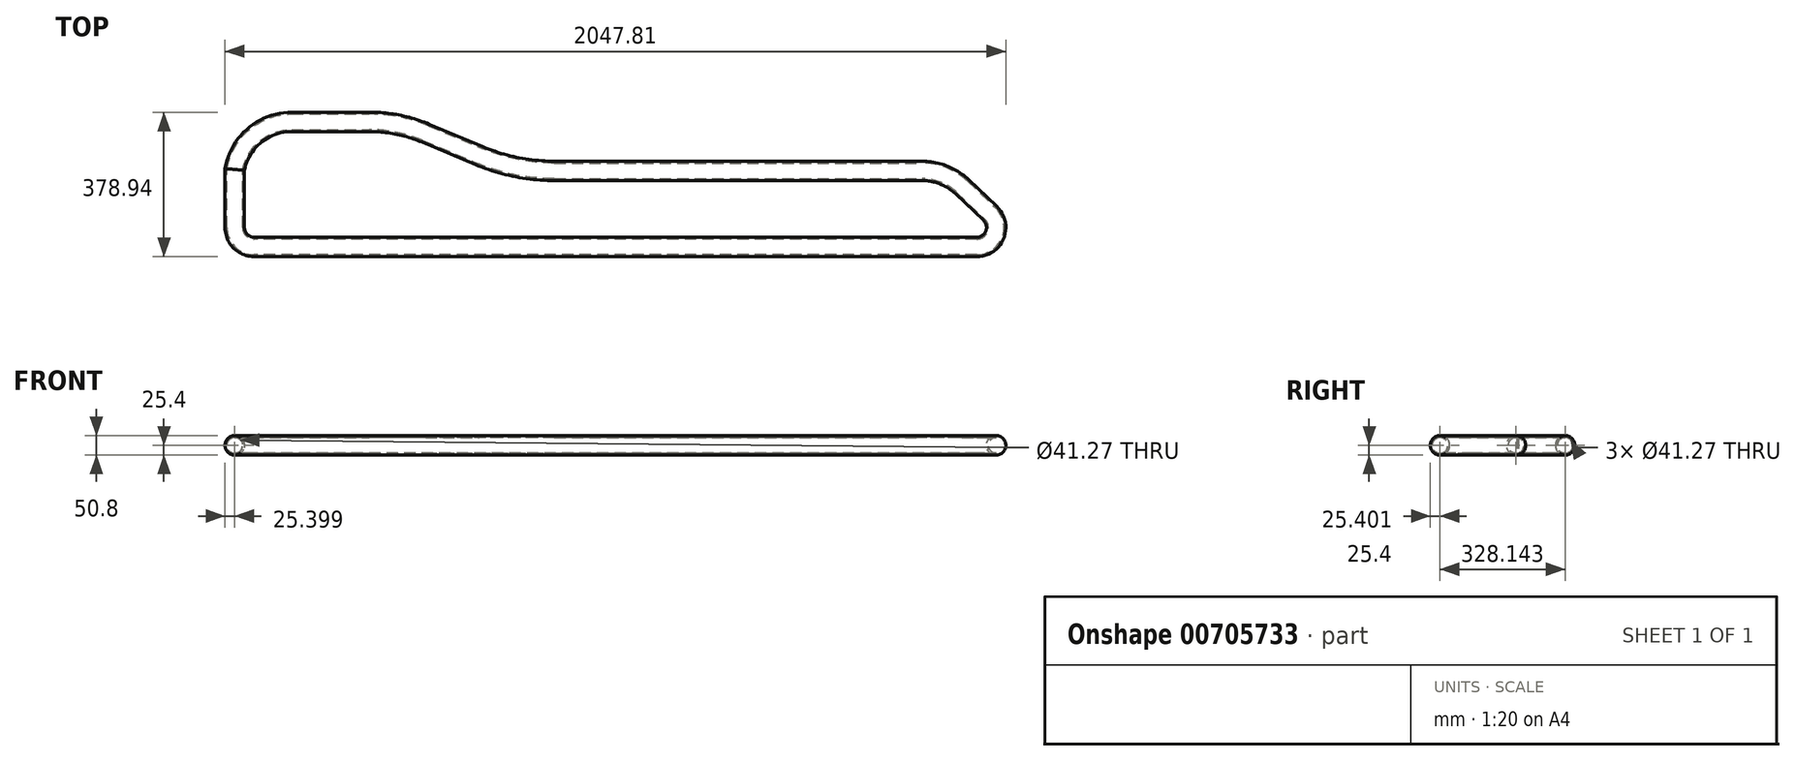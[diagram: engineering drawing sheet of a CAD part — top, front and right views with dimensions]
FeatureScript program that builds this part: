
annotation { "Feature Type Name" : "Feature", "Feature Type Description" : "" }
export const myFeature = defineFeature(function(context is Context, id is Id, definition is map)
    precondition{}
    {
        {
            var Q0;
            Q0=qCreatedBy(makeId("Top.planeOp"),FACE);
            var sketch = newSketch(context, id + "F0", { "sketchPlane" : qUnion([Q0])});
            skLineSegment(sketch, "E0", {"start": v(1142.94, -111.89) * mm, "end": v(1069.28, -41.91) * mm});
            skLineSegment(sketch, "E1", {"start": v(964.31, 0) * mm, "end": v(0, 0) * mm});
            skLineSegment(sketch, "E2", {"start": v(-485.15, 128.62) * mm, "end": v(-688.35, 128.62) * mm});
            skPoint(sketch, "E3.visualSharp", {"position": v(1025.16, 0) * mm});
            skArc(sketch, "E3.filletArc", {"start": v(1069.28, -41.91) * mm, "mid": v(1020.83, -10.87) * mm, "end": v(964.31, 0) * mm});
            skPoint(sketch, "E4.visualSharp", {"position": v(-837.22, 128.62) * mm});
            skArc(sketch, "E4.filletArc", {"start": v(-688.35, 128.62) * mm, "mid": v(-785.93, 93.3) * mm, "end": v(-838.26, 3.68) * mm});
            skLineSegment(sketch, "E5", {"start": v(-196.96, 39.74) * mm, "end": v(-337.44, 98.82) * mm});
            skPoint(sketch, "E6.visualSharp", {"position": v(-102.49, 0) * mm});
            skArc(sketch, "E6.filletArc", {"start": v(-196.96, 39.74) * mm, "mid": v(-100.46, 10.03) * mm, "end": v(0, 0) * mm});
            skPoint(sketch, "E7.visualSharp", {"position": v(-408.29, 128.62) * mm});
            skArc(sketch, "E7.filletArc", {"start": v(-337.44, 98.82) * mm, "mid": v(-409.8, 121.1) * mm, "end": v(-485.15, 128.62) * mm});
            skLineSegment(sketch, "E8", {"start": v(-838.26, 3.68) * mm, "end": v(-838.26, -148.72) * mm});
            skLineSegment(sketch, "E9", {"start": v(-787.46, -199.52) * mm, "end": v(1107.95, -199.52) * mm});
            skPoint(sketch, "E10.visualSharp", {"position": v(-838.26, -199.52) * mm});
            skArc(sketch, "E10.filletArc", {"start": v(-838.26, -148.72) * mm, "mid": v(-823.38, -184.64) * mm, "end": v(-787.46, -199.52) * mm});
            skPoint(sketch, "E11.visualSharp", {"position": v(1235.18, -199.52) * mm});
            skArc(sketch, "E11.filletArc", {"start": v(1240.54, -199.52) * mm, "mid": v(1242.52, -202.45) * mm, "end": v(1239.07, -203.21) * mm});
            skArc(sketch, "E12.filletArc", {"start": v(1107.95, -199.52) * mm, "mid": v(1155.13, -167.56) * mm, "end": v(1142.94, -111.89) * mm});
            skSolve(sketch);
        }
        {
            var Q0;
            Q0=qCreatedBy(makeId("Right.planeOp"),FACE);
            var sketch = newSketch(context, id + "F1", { "sketchPlane" : qUnion([Q0])});
            skCircle(sketch, "E13", {"center": v(0, 0) * mm, "radius": 25.4 * mm});
            skCircle(sketch, "E14", {"center": v(0, 0) * mm, "radius": 20.64 * mm});
            skSolve(sketch);
        }
        {
            var Q0;
            Q0=makeQuery(id+"F1.imprint","IMPRINT",FACE,{"disambiguationData":[TD([[makeQuery(id+"F1.imprint","IMPRINT",EDGE,{"derivedFrom":sQuery(id+"F1.wireOp",EDGE,"E13")}),1.0]])]});
            var Q1;
            Q1=sQuery(id+"F0.wireOp",EDGE,"E1");
            var Q2;
            Q2=sQuery(id+"F0.wireOp",EDGE,"E0");
            var Q3;
            Q3=sQuery(id+"F0.wireOp",EDGE,"E3.filletArc");
            var Q4;
            Q4=sQuery(id+"F0.wireOp",EDGE,"E6.filletArc");
            var Q5;
            Q5=sQuery(id+"F0.wireOp",EDGE,"E7.filletArc");
            var Q6;
            Q6=sQuery(id+"F0.wireOp",EDGE,"E2");
            var Q7;
            Q7=sQuery(id+"F0.wireOp",EDGE,"E4.filletArc");
            var Q8;
            Q8=sQuery(id+"F0.wireOp",EDGE,"E8");
            var Q9;
            Q9=sQuery(id+"F0.wireOp",EDGE,"E10.filletArc");
            var Q10;
            Q10=sQuery(id+"F0.wireOp",EDGE,"E9");
            var Q11;
            Q11=sQuery(id+"F0.wireOp",EDGE,"E5");
            var Q12;
            Q12=sQuery(id+"F0.wireOp",EDGE,"E12.filletArc");
            sweep(context, id + "F2", {"profiles" : qUnion([Q0]), "path" : qUnion([Q1, Q2, Q3, Q4, Q5, Q6, Q7, Q8, Q9, Q10, Q11, Q12])});
        }
    });
